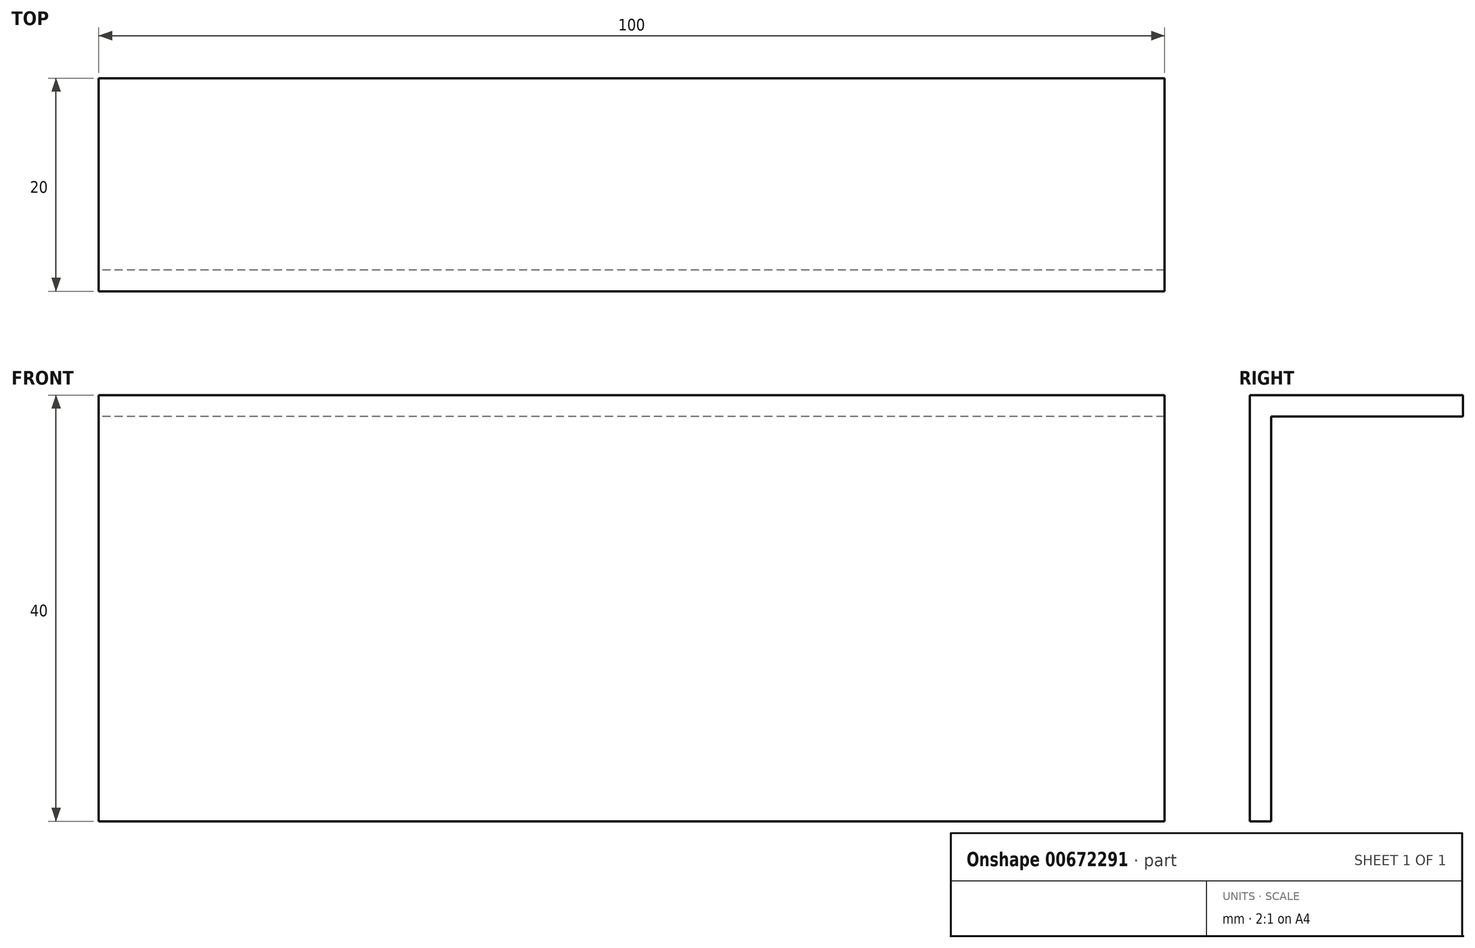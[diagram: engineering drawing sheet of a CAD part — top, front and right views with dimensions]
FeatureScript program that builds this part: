
annotation { "Feature Type Name" : "Feature", "Feature Type Description" : "" }
export const myFeature = defineFeature(function(context is Context, id is Id, definition is map)
    precondition{}
    {
        {
            var Q0;
            Q0=qCreatedBy(makeId("Right.planeOp"),FACE);
            var sketch = newSketch(context, id + "F0", { "sketchPlane" : qUnion([Q0])});
            skLineSegment(sketch, "E0", {"start": v(0, 0) * mm, "end": v(20, 0) * mm});
            skLineSegment(sketch, "E1", {"start": v(20, 0) * mm, "end": v(20, -2) * mm});
            skLineSegment(sketch, "E2", {"start": v(20, -2) * mm, "end": v(2, -2) * mm});
            skLineSegment(sketch, "E3", {"start": v(2, -2) * mm, "end": v(2, -40) * mm});
            skLineSegment(sketch, "E4", {"start": v(0, 0) * mm, "end": v(0, -40) * mm});
            skLineSegment(sketch, "E5", {"start": v(0, -40) * mm, "end": v(2, -40) * mm});
            skSolve(sketch);
        }
        {
            var Q0;
            Q0 = qSketchRegion(id + "F0", true);
            extrude(context, id + "F1", {"entities" : qUnion([Q0]), "depth" : 100 * mm, "offsetDistance" : 25 * mm});
        }
    });
